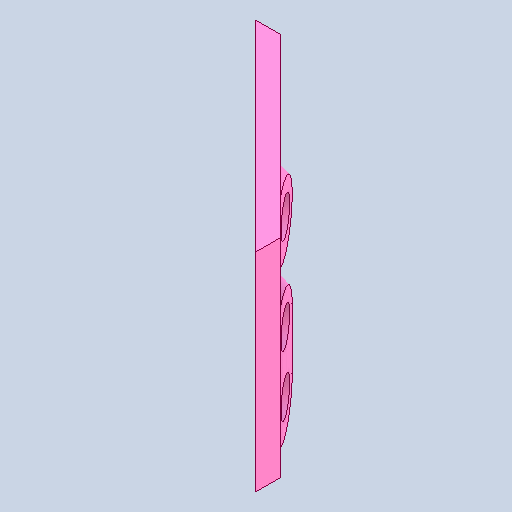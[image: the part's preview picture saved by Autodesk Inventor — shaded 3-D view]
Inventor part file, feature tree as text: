
AUTODESK INVENTOR PART (.ipt)
format: ipt  version: 2023.1 (Build 271208000, 208)  size: 483,328 bytes
history: native  units: mm
features: projected_geometry x14, extrude x13, sketch x8, other x2, plane x1, chamfer x1, reference x1
ambient origin geometry x8: Origin, YZ Plane, XZ Plane, XY Plane, X Axis, Y Axis, Z Axis, Center Point
bodies: Solid1 (feature_tree)
feature tree (40):
  plane  "Work Plane1"
  extrude  "Extrusion1"  Depth=0.075mm
  sketch  "Sketch2"  dims[d6=135.0deg d7=30.0mm d8=0.0mm]
  extrude  "Extrusion2"  Depth=30.0mm TaperAngle=0.0deg
  extrude  "Extrusion3"  Depth=2.5mm
  sketch  "Sketch3"  dims[d9=2.5mm d10=2.5mm]
  extrude  "Extrusion4"  Depth=30.0mm TaperAngle=0.0deg
  extrude  "Extrusion5"  Depth=17.5mm
  sketch  "Sketch4"  dims[d13=2.5mm d14=30.0mm d15=0.0mm]
  extrude  "Extrusion6"  Depth=2.5mm
  extrude  "Extrusion7"  Depth=4.25mm TaperAngle=0.0deg
  sketch  "Sketch7"  dims[d16=20.0mm d17=17.5mm]
  extrude  "Extrusion10"  Depth=2.5mm
  extrude  "Extrusion11"  Depth=100.0mm TaperAngle=0.0deg
  sketch  "Sketch8"  dims[d18=5.175mm d19=2.5mm]
  extrude  "Extrusion12"  Depth=15.0mm TaperAngle=0.0deg
  extrude  "Extrusion13"  Depth=8.75mm
  extrude  "Extrusion14"  Depth=10.0mm TaperAngle=0.0deg
  chamfer  "Chamfer1"  Distance=1.745329mm
  extrude  "Extrusion15"  Depth=2.5mm TaperAngle=0.0deg
  sketch  "Sketch1"  dims[d3=2.5mm d4=0.0mm d5=0.075mm]
  reference  "Reference6"
  projected_geometry  "Projected Loop1"
  projected_geometry  "Projected Loop3"
  projected_geometry  "Projected Loop4"
  projected_geometry  "Projected Loop6"
  sketch  "Sketch9"  dims[d20=50.0mm d21=0.0mm d23=4.25mm d24=0.0mm]
  projected_geometry  "Projected Loop7"
  sketch  "Sketch10"  dims[d25=5.175mm d26=2.5mm d27=100.0mm d28=0.0mm d29=15.0mm d30=0.0mm d37=8.75mm d39=10.0mm d40=0.0mm d46=1.745329mm d47=2.5mm d48=0.0mm d68=30.0mm d69=0.0mm d70=0.25mm d71=0.25mm d72=5.075mm d73=29.670597mm d74=2.0mm d75=5.075mm d76=29.670597mm d77=2.0mm d78=1.5mm d79=1.5mm d80=5.075mm d81=0.0mm d86=5.075mm d87=1.5mm d88=20.0mm d90=8.75mm d91=10.0mm d93=10.0mm d95=1.5mm d96=0.0mm d97=1.5mm d98=0.0mm d99=5.075mm d100=1.5mm d101=1.5mm d102=0.0mm d103=1.21mm d104=2.0mm d105=45.0deg d109=50.0mm d110=0.0mm d82=0.5mm d83=0.872665mm d84=0.5mm d85=0.872665mm]
  projected_geometry  "Projected Loop8"
  projected_geometry  "Projected Loop9"
  projected_geometry  "Projected Loop10"
  projected_geometry  "Projected Loop11"
  projected_geometry  "Projected Loop12"
  projected_geometry  "Projected Loop13"
  projected_geometry  "Projected Loop14"
  projected_geometry  "Projected Loop15"
  projected_geometry  "Projected Loop16"
  other  "Cube 1x1 V5.iam"
  other  "Cube 1x1 Bottom V5:1"
